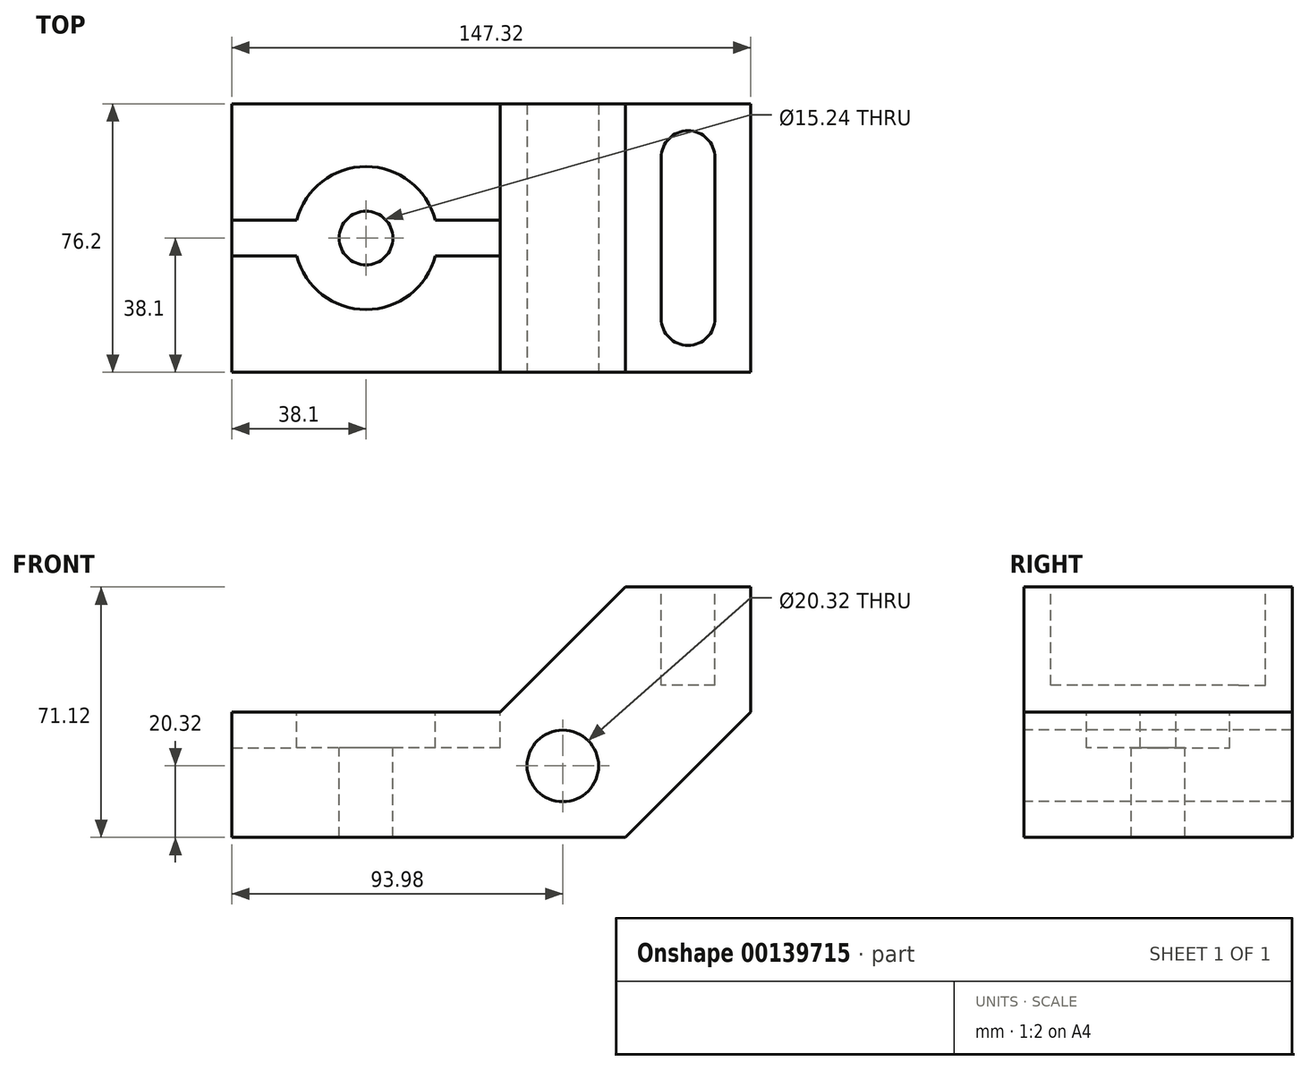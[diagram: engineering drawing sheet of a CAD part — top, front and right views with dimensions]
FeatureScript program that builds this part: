
annotation { "Feature Type Name" : "Feature", "Feature Type Description" : "" }
export const myFeature = defineFeature(function(context is Context, id is Id, definition is map)
    precondition{}
    {
        {
            var Q0;
            Q0=qCreatedBy(makeId("Top.planeOp"),FACE);
            var sketch = newSketch(context, id + "F0", { "sketchPlane" : qUnion([Q0])});
            skLineSegment(sketch, "E0", {"start": v(0, 76.2) * mm, "end": v(0, 0) * mm});
            skLineSegment(sketch, "E1", {"start": v(0, 0) * mm, "end": v(147.32, 0) * mm});
            skLineSegment(sketch, "E2", {"start": v(147.32, 0) * mm, "end": v(147.32, 76.2) * mm});
            skLineSegment(sketch, "E3", {"start": v(147.32, 76.2) * mm, "end": v(0, 76.2) * mm});
            skSolve(sketch);
        }
        {
            var Q0;
            Q0 = qSketchRegion(id + "F0", true);
            extrude(context, id + "F1", {"entities" : qUnion([Q0]), "depth" : 71.12 * mm});
        }
        {
            var Q0;
            Q0=makeQuery(id+"F1.opExtrude","SWEPT_FACE",FACE,{"disambiguationData":[OSD([sQuery(id+"F0.wireOp",EDGE,"E1")])]});
            var sketch = newSketch(context, id + "F2", { "sketchPlane" : qUnion([Q0])});
            skLineSegment(sketch, "E4", {"start": v(147.32, 35.56) * mm, "end": v(147.32, 0) * mm});
            skLineSegment(sketch, "E5", {"start": v(147.32, 0) * mm, "end": v(111.76, 0) * mm});
            skLineSegment(sketch, "E6", {"start": v(111.76, 0) * mm, "end": v(147.32, 35.56) * mm});
            skLineSegment(sketch, "E7", {"start": v(111.76, 71.12) * mm, "end": v(76.2, 35.56) * mm});
            skLineSegment(sketch, "E8", {"start": v(76.2, 35.56) * mm, "end": v(0, 35.56) * mm});
            skLineSegment(sketch, "E9", {"start": v(0, 35.56) * mm, "end": v(0, 71.12) * mm});
            skLineSegment(sketch, "E10", {"start": v(0, 71.12) * mm, "end": v(111.76, 71.12) * mm});
            skSolve(sketch);
        }
        {
            var Q0;
            Q0 = qSketchRegion(id + "F2", true);
            extrude(context, id + "F3", {"entities" : qUnion([Q0]), "operationType" : NewBodyOperationType.REMOVE, "endBound" : BoundingType.THROUGH_ALL, "oppositeDirection" : true, "depth" : 25.4 * mm});
        }
        {
            var Q0;
            Q0=makeQuery(id+"F1.opExtrude","CAP_FACE",FACE,{"disambiguationData":[OSD([sQuery(id+"F0.wireOp",EDGE,"E0"),sQuery(id+"F0.wireOp",EDGE,"E1"),sQuery(id+"F0.wireOp",EDGE,"E2"),sQuery(id+"F0.wireOp",EDGE,"E3")])],"isStart":false});
            var sketch = newSketch(context, id + "F4", { "sketchPlane" : qUnion([Q0])});
            skLineSegment(sketch, "E11", {"start": v(137.16, 60.96) * mm, "end": v(137.16, 15.24) * mm});
            skLineSegment(sketch, "E12", {"start": v(121.92, 60.96) * mm, "end": v(121.92, 15.24) * mm});
            skArc(sketch, "E13", {"start": v(121.92, 60.96) * mm, "mid": v(129.54, 68.58) * mm, "end": v(137.16, 60.96) * mm});
            skArc(sketch, "E14", {"start": v(121.92, 15.24) * mm, "mid": v(129.54, 7.62) * mm, "end": v(137.16, 15.24) * mm});
            skSolve(sketch);
        }
        {
            var Q0;
            Q0 = qSketchRegion(id + "F4", true);
            extrude(context, id + "F5", {"entities" : qUnion([Q0]), "operationType" : NewBodyOperationType.REMOVE, "oppositeDirection" : true, "depth" : 27.94 * mm});
        }
        {
            var Q0;
            Q0=makeQuery(id+"F1.opExtrude","SWEPT_FACE",FACE,{"disambiguationData":[OSD([sQuery(id+"F0.wireOp",EDGE,"E1")])]});
            var sketch = newSketch(context, id + "F6", { "sketchPlane" : qUnion([Q0])});
            skCircle(sketch, "E15", {"center": v(93.98, 20.32) * mm, "radius": 10.16 * mm});
            skSolve(sketch);
        }
        {
            var Q0;
            Q0 = qSketchRegion(id + "F6", true);
            extrude(context, id + "F7", {"entities" : qUnion([Q0]), "operationType" : NewBodyOperationType.REMOVE, "endBound" : BoundingType.THROUGH_ALL, "oppositeDirection" : true, "depth" : 25.4 * mm});
        }
        {
            var Q0;
            Q0=makeQuery(id+"F3.boolean.opBoolean","COPY",FACE,{"derivedFrom":makeQuery(id+"F3.opExtrude","SWEPT_FACE",FACE,{"disambiguationData":[OSD([sQuery(id+"F2.wireOp",EDGE,"E8")])]})});
            var sketch = newSketch(context, id + "F8", { "sketchPlane" : qUnion([Q0])});
            skPoint(sketch, "E16", {"position": v(38.1, 38.1) * mm});
            skSolve(sketch);
        }
        {
            var Q0;
            Q0=sQuery(id+"F8.wireOp",VERTEX,"E16");
            var Q1;
            Q1=makeQuery(id+"F1.opExtrude","SWEPT_BODY",BODY,{"disambiguationData":[OSD([sQuery(id+"F0.wireOp",EDGE,"E0"),sQuery(id+"F0.wireOp",EDGE,"E1"),sQuery(id+"F0.wireOp",EDGE,"E2"),sQuery(id+"F0.wireOp",EDGE,"E3")])]});
            hole(context, id + "F9", {"style" : HoleStyle.C_BORE, "endStyle" : HoleEndStyle.THROUGH, "holeDiameter" : 15.24 * mm, "cBoreDiameter" : 40.64 * mm, "cBoreDepth" : 10.16 * mm, "locations" : qUnion([Q0]), "scope" : qUnion([Q1]), "isTappedThrough" : true});
        }
        {
            var Q0;
            Q0=makeQuery(id+"F3.boolean.opBoolean","COPY",FACE,{"derivedFrom":makeQuery(id+"F3.opExtrude","SWEPT_FACE",FACE,{"disambiguationData":[OSD([sQuery(id+"F2.wireOp",EDGE,"E8")])]})});
            var sketch = newSketch(context, id + "F10", { "sketchPlane" : qUnion([Q0])});
            skLineSegment(sketch, "E17", {"start": v(0, 43.18) * mm, "end": v(76.2, 43.18) * mm});
            skLineSegment(sketch, "E18", {"start": v(76.2, 43.18) * mm, "end": v(76.2, 33.02) * mm});
            skLineSegment(sketch, "E19", {"start": v(76.2, 33.02) * mm, "end": v(0, 33.02) * mm});
            skLineSegment(sketch, "E20", {"start": v(0, 33.02) * mm, "end": v(0, 43.18) * mm});
            skSolve(sketch);
        }
        {
            var Q0;
            Q0 = qSketchRegion(id + "F10", true);
            extrude(context, id + "F11", {"entities" : qUnion([Q0]), "operationType" : NewBodyOperationType.REMOVE, "oppositeDirection" : true, "depth" : 10.16 * mm});
        }
    });
